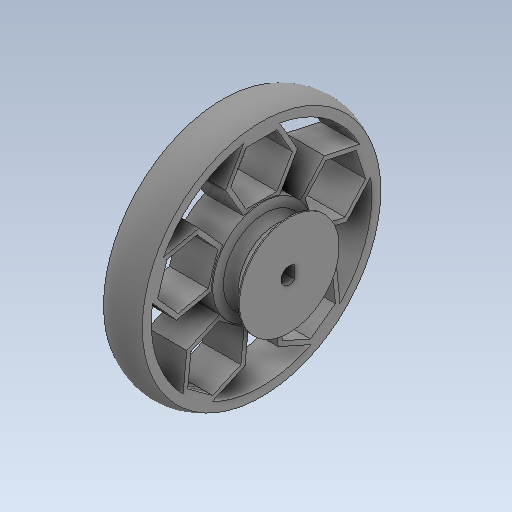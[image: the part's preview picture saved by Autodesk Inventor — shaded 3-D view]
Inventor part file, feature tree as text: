
AUTODESK INVENTOR PART (.ipt)
format: ipt  version: 2020 (Build 240168000, 168)  size: 465,408 bytes
history: native  units: in
note: dims shown in document units (in); Inventor stores cm internally (conversion verified against a paired STEP export)
features: sketch x4, extrude x2, revolve x2, projected_geometry x1
ambient origin geometry x8: Origin, YZ Plane, XZ Plane, XY Plane, X Axis, Y Axis, Z Axis, Center Point
bodies: Solid1 (feature_tree)
feature tree (9):
  extrude  "Extrusion1"  Depth=0.0394in
  sketch  "Sketch3"  dims[d6=0.7087in d7=0.1969in]
  revolve  "Revolution1"  [1 undecoded]
  extrude  "Extrusion2"  Depth=0.1969in
  revolve  "Revolution2"  [1 undecoded]
  sketch  "Sketch1"  dims[d0=0.1181in d1=0.0394in]
  sketch  "Sketch2"  dims[d3=1.6929in d4=0.1181in]
  projected_geometry  "Projected Loop1"
  sketch  "Sketch4"  dims[d8=0.0in d9=1.6929in d10=0.063in d11=0.0315in d16=0.2756in d17=0.0in d19=360.0deg d20=0.0984in d24=0.0394in d25=90.0deg d26=45.0deg d28=0.0079in d29=1.9685in d31=360.0deg]
note: 2 required parameter values undecoded (feature->parameter linkage not recoverable at this tier; creation-order binding heuristic only, values carry confidence <= 0.55)
